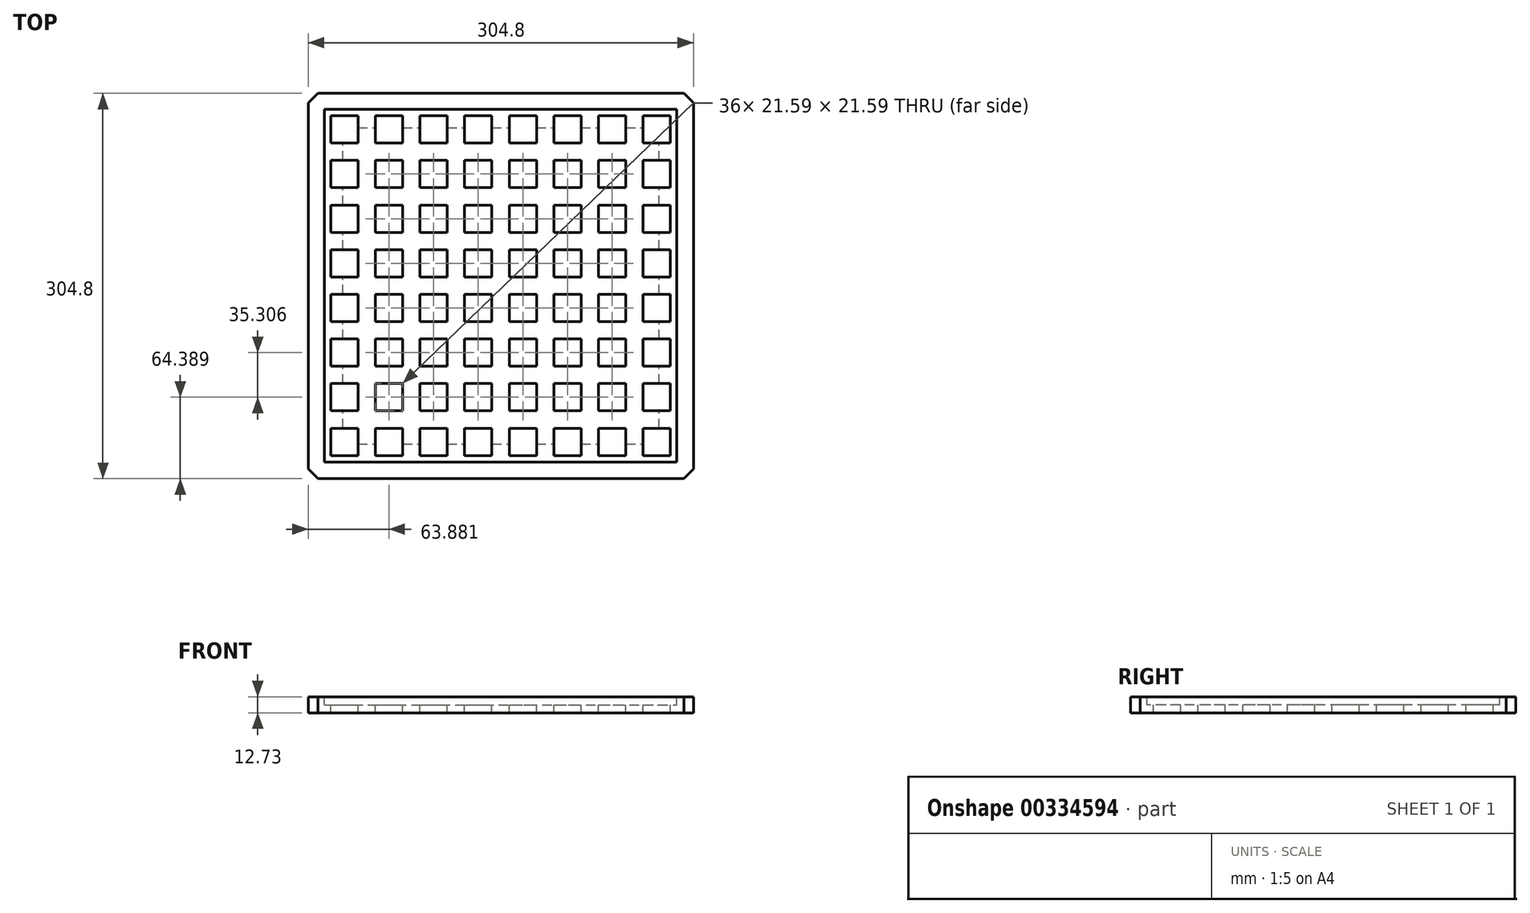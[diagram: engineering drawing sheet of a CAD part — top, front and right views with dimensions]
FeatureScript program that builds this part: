
annotation { "Feature Type Name" : "Feature", "Feature Type Description" : "" }
export const myFeature = defineFeature(function(context is Context, id is Id, definition is map)
    precondition{}
    {
        {
            var Q0;
            Q0=qCreatedBy(makeId("Top.planeOp"),FACE);
            var sketch = newSketch(context, id + "F0", { "sketchPlane" : qUnion([Q0])});
            skLineSegment(sketch, "E0.bottom", {"start": v(-152.4, 152.4) * mm, "end": v(152.4, 152.4) * mm});
            skLineSegment(sketch, "E0.top", {"start": v(-152.4, -152.4) * mm, "end": v(152.4, -152.4) * mm});
            skLineSegment(sketch, "E0.left", {"start": v(-152.4, 152.4) * mm, "end": v(-152.4, -152.4) * mm});
            skLineSegment(sketch, "E0.right", {"start": v(152.4, 152.4) * mm, "end": v(152.4, -152.4) * mm});
            skPoint(sketch, "E0.middle", {"position": v(0, 0) * mm});
            skSolve(sketch);
        }
        {
            var Q0;
            Q0=makeQuery(id+"F0.imprint","IMPRINT",FACE,{"disambiguationData":[TD([[makeQuery(id+"F0.imprint","IMPRINT",EDGE,{"derivedFrom":sQuery(id+"F0.wireOp",EDGE,"E0.bottom")}),-1.0]])]});
            extrude(context, id + "F1", {"entities" : qUnion([Q0]), "depth" : 12.7 * mm});
        }
        {
            var Q0;
            Q0=makeQuery(id+"F1.opExtrude","CAP_FACE",FACE,{"disambiguationData":[OSD([sQuery(id+"F0.wireOp",EDGE,"E0.bottom"),sQuery(id+"F0.wireOp",EDGE,"E0.top"),sQuery(id+"F0.wireOp",EDGE,"E0.left"),sQuery(id+"F0.wireOp",EDGE,"E0.right")])],"isStart":false});
            var sketch = newSketch(context, id + "F2", { "sketchPlane" : qUnion([Q0])});
            skLineSegment(sketch, "E1.top", {"start": v(-139.7, -139.7) * mm, "end": v(139.7, -139.7) * mm, "construction": true});
            skLineSegment(sketch, "E1.right", {"start": v(139.7, 139.7) * mm, "end": v(139.7, -139.7) * mm, "construction": true});
            skPoint(sketch, "E1.middle", {"position": v(0, 0) * mm});
            skLineSegment(sketch, "E2.bottom", {"start": v(-139.7, 139.7) * mm, "end": v(-107.95, 139.7) * mm});
            skLineSegment(sketch, "E2.top", {"start": v(-139.7, 107.95) * mm, "end": v(-107.95, 107.95) * mm});
            skLineSegment(sketch, "E2.left", {"start": v(-139.7, 139.7) * mm, "end": v(-139.7, 107.95) * mm});
            skLineSegment(sketch, "E2.right", {"start": v(-107.95, 139.7) * mm, "end": v(-107.95, 107.95) * mm});
            skLineSegment(sketch, "E3.1.0.0", {"start": v(-104.4, 139.7) * mm, "end": v(-72.64, 139.7) * mm});
            skLineSegment(sketch, "E3.1.0.1", {"start": v(-104.4, 107.95) * mm, "end": v(-72.64, 107.95) * mm});
            skLineSegment(sketch, "E3.1.0.2", {"start": v(-104.4, 139.7) * mm, "end": v(-104.4, 107.95) * mm});
            skLineSegment(sketch, "E3.1.0.3", {"start": v(-72.64, 139.7) * mm, "end": v(-72.64, 107.95) * mm});
            skLineSegment(sketch, "E3.2.0.0", {"start": v(-69.09, 139.7) * mm, "end": v(-37.34, 139.7) * mm});
            skLineSegment(sketch, "E3.2.0.1", {"start": v(-69.09, 107.95) * mm, "end": v(-37.34, 107.95) * mm});
            skLineSegment(sketch, "E3.2.0.2", {"start": v(-69.09, 139.7) * mm, "end": v(-69.09, 107.95) * mm});
            skLineSegment(sketch, "E3.2.0.3", {"start": v(-37.34, 139.7) * mm, "end": v(-37.34, 107.95) * mm});
            skLineSegment(sketch, "E3.3.0.0", {"start": v(-33.78, 139.7) * mm, "end": v(-2.03, 139.7) * mm});
            skLineSegment(sketch, "E3.3.0.1", {"start": v(-33.78, 107.95) * mm, "end": v(-2.03, 107.95) * mm});
            skLineSegment(sketch, "E3.3.0.2", {"start": v(-33.78, 139.7) * mm, "end": v(-33.78, 107.95) * mm});
            skLineSegment(sketch, "E3.3.0.3", {"start": v(-2.03, 139.7) * mm, "end": v(-2.03, 107.95) * mm});
            skLineSegment(sketch, "E3.4.0.0", {"start": v(1.52, 139.7) * mm, "end": v(33.27, 139.7) * mm});
            skLineSegment(sketch, "E3.4.0.1", {"start": v(1.52, 107.95) * mm, "end": v(33.27, 107.95) * mm});
            skLineSegment(sketch, "E3.4.0.2", {"start": v(1.52, 139.7) * mm, "end": v(1.52, 107.95) * mm});
            skLineSegment(sketch, "E3.4.0.3", {"start": v(33.27, 139.7) * mm, "end": v(33.27, 107.95) * mm});
            skLineSegment(sketch, "E3.5.0.0", {"start": v(36.83, 139.7) * mm, "end": v(68.58, 139.7) * mm});
            skLineSegment(sketch, "E3.5.0.1", {"start": v(36.83, 107.95) * mm, "end": v(68.58, 107.95) * mm});
            skLineSegment(sketch, "E3.5.0.2", {"start": v(36.83, 139.7) * mm, "end": v(36.83, 107.95) * mm});
            skLineSegment(sketch, "E3.5.0.3", {"start": v(68.58, 139.7) * mm, "end": v(68.58, 107.95) * mm});
            skLineSegment(sketch, "E3.6.0.0", {"start": v(72.14, 139.7) * mm, "end": v(103.89, 139.7) * mm});
            skLineSegment(sketch, "E3.6.0.1", {"start": v(72.14, 107.95) * mm, "end": v(103.89, 107.95) * mm});
            skLineSegment(sketch, "E3.6.0.2", {"start": v(72.14, 139.7) * mm, "end": v(72.14, 107.95) * mm});
            skLineSegment(sketch, "E3.6.0.3", {"start": v(103.89, 139.7) * mm, "end": v(103.89, 107.95) * mm});
            skLineSegment(sketch, "E3.7.0.0", {"start": v(107.44, 139.7) * mm, "end": v(139.2, 139.7) * mm});
            skLineSegment(sketch, "E3.7.0.1", {"start": v(107.44, 107.95) * mm, "end": v(139.2, 107.95) * mm});
            skLineSegment(sketch, "E3.7.0.2", {"start": v(107.44, 139.7) * mm, "end": v(107.44, 107.95) * mm});
            skLineSegment(sketch, "E3.7.0.3", {"start": v(139.2, 139.7) * mm, "end": v(139.2, 107.95) * mm});
            skLineSegment(sketch, "E3.direction1", {"start": v(-139.7, 107.95) * mm, "end": v(-104.4, 107.95) * mm, "construction": true});
            skLineSegment(sketch, "E4.0.1.0", {"start": v(-69.09, 104.4) * mm, "end": v(-37.34, 104.4) * mm});
            skLineSegment(sketch, "E4.0.1.1", {"start": v(-72.64, 104.4) * mm, "end": v(-72.64, 72.64) * mm});
            skLineSegment(sketch, "E4.0.1.2", {"start": v(1.52, 104.4) * mm, "end": v(33.27, 104.4) * mm});
            skLineSegment(sketch, "E4.0.1.3", {"start": v(-139.7, 72.64) * mm, "end": v(-104.4, 72.64) * mm, "construction": true});
            skLineSegment(sketch, "E4.0.1.4", {"start": v(-104.4, 104.4) * mm, "end": v(-104.4, 72.64) * mm});
            skLineSegment(sketch, "E4.0.1.5", {"start": v(-69.09, 72.64) * mm, "end": v(-37.34, 72.64) * mm});
            skLineSegment(sketch, "E4.0.1.6", {"start": v(107.44, 72.64) * mm, "end": v(139.2, 72.64) * mm});
            skLineSegment(sketch, "E4.0.1.7", {"start": v(36.83, 104.4) * mm, "end": v(68.58, 104.4) * mm});
            skLineSegment(sketch, "E4.0.1.8", {"start": v(68.58, 104.4) * mm, "end": v(68.58, 72.64) * mm});
            skLineSegment(sketch, "E4.0.1.9", {"start": v(-69.09, 104.4) * mm, "end": v(-69.09, 72.64) * mm});
            skLineSegment(sketch, "E4.0.1.10", {"start": v(-104.4, 72.64) * mm, "end": v(-72.64, 72.64) * mm});
            skLineSegment(sketch, "E4.0.1.11", {"start": v(-104.4, 104.4) * mm, "end": v(-72.64, 104.4) * mm});
            skLineSegment(sketch, "E4.0.1.12", {"start": v(-107.95, 104.4) * mm, "end": v(-107.95, 72.64) * mm});
            skLineSegment(sketch, "E4.0.1.13", {"start": v(-139.7, 104.4) * mm, "end": v(-139.7, 72.64) * mm});
            skLineSegment(sketch, "E4.0.1.14", {"start": v(-139.7, 104.4) * mm, "end": v(-107.95, 104.4) * mm});
            skLineSegment(sketch, "E4.0.1.15", {"start": v(-33.78, 72.64) * mm, "end": v(-2.03, 72.64) * mm});
            skLineSegment(sketch, "E4.0.1.16", {"start": v(-33.78, 104.4) * mm, "end": v(-2.03, 104.4) * mm});
            skLineSegment(sketch, "E4.0.1.17", {"start": v(-37.34, 104.4) * mm, "end": v(-37.34, 72.64) * mm});
            skLineSegment(sketch, "E4.0.1.18", {"start": v(1.52, 72.64) * mm, "end": v(33.27, 72.64) * mm});
            skLineSegment(sketch, "E4.0.1.19", {"start": v(72.14, 104.4) * mm, "end": v(103.89, 104.4) * mm});
            skLineSegment(sketch, "E4.0.1.20", {"start": v(-2.03, 104.4) * mm, "end": v(-2.03, 72.64) * mm});
            skLineSegment(sketch, "E4.0.1.21", {"start": v(139.2, 104.4) * mm, "end": v(139.2, 72.64) * mm});
            skLineSegment(sketch, "E4.0.1.22", {"start": v(33.27, 104.4) * mm, "end": v(33.27, 72.64) * mm});
            skLineSegment(sketch, "E4.0.1.23", {"start": v(107.44, 104.4) * mm, "end": v(139.2, 104.4) * mm});
            skLineSegment(sketch, "E4.0.1.24", {"start": v(36.83, 104.4) * mm, "end": v(36.83, 72.64) * mm});
            skLineSegment(sketch, "E4.0.1.25", {"start": v(72.14, 104.4) * mm, "end": v(72.14, 72.64) * mm});
            skLineSegment(sketch, "E4.0.1.26", {"start": v(72.14, 72.64) * mm, "end": v(103.89, 72.64) * mm});
            skLineSegment(sketch, "E4.0.1.27", {"start": v(36.83, 72.64) * mm, "end": v(68.58, 72.64) * mm});
            skLineSegment(sketch, "E4.0.1.28", {"start": v(103.89, 104.4) * mm, "end": v(103.89, 72.64) * mm});
            skLineSegment(sketch, "E4.0.1.29", {"start": v(1.52, 104.4) * mm, "end": v(1.52, 72.64) * mm});
            skLineSegment(sketch, "E4.0.1.30", {"start": v(107.44, 104.4) * mm, "end": v(107.44, 72.64) * mm});
            skLineSegment(sketch, "E4.0.1.31", {"start": v(-33.78, 104.4) * mm, "end": v(-33.78, 72.64) * mm});
            skLineSegment(sketch, "E4.0.1.32", {"start": v(-139.7, 72.64) * mm, "end": v(-107.95, 72.64) * mm});
            skLineSegment(sketch, "E4.0.2.0", {"start": v(-69.09, 69.09) * mm, "end": v(-37.34, 69.09) * mm});
            skLineSegment(sketch, "E4.0.2.1", {"start": v(-72.64, 69.09) * mm, "end": v(-72.64, 37.34) * mm});
            skLineSegment(sketch, "E4.0.2.2", {"start": v(1.52, 69.09) * mm, "end": v(33.27, 69.09) * mm});
            skLineSegment(sketch, "E4.0.2.3", {"start": v(-139.7, 37.34) * mm, "end": v(-104.4, 37.34) * mm, "construction": true});
            skLineSegment(sketch, "E4.0.2.4", {"start": v(-104.4, 69.09) * mm, "end": v(-104.4, 37.34) * mm});
            skLineSegment(sketch, "E4.0.2.5", {"start": v(-69.09, 37.34) * mm, "end": v(-37.34, 37.34) * mm});
            skLineSegment(sketch, "E4.0.2.6", {"start": v(107.44, 37.34) * mm, "end": v(139.2, 37.34) * mm});
            skLineSegment(sketch, "E4.0.2.7", {"start": v(36.83, 69.09) * mm, "end": v(68.58, 69.09) * mm});
            skLineSegment(sketch, "E4.0.2.8", {"start": v(68.58, 69.09) * mm, "end": v(68.58, 37.34) * mm});
            skLineSegment(sketch, "E4.0.2.9", {"start": v(-69.09, 69.09) * mm, "end": v(-69.09, 37.34) * mm});
            skLineSegment(sketch, "E4.0.2.10", {"start": v(-104.4, 37.34) * mm, "end": v(-72.64, 37.34) * mm});
            skLineSegment(sketch, "E4.0.2.11", {"start": v(-104.4, 69.09) * mm, "end": v(-72.64, 69.09) * mm});
            skLineSegment(sketch, "E4.0.2.12", {"start": v(-107.95, 69.09) * mm, "end": v(-107.95, 37.34) * mm});
            skLineSegment(sketch, "E4.0.2.13", {"start": v(-139.7, 69.09) * mm, "end": v(-139.7, 37.34) * mm});
            skLineSegment(sketch, "E4.0.2.14", {"start": v(-139.7, 69.09) * mm, "end": v(-107.95, 69.09) * mm});
            skLineSegment(sketch, "E4.0.2.15", {"start": v(-33.78, 37.34) * mm, "end": v(-2.03, 37.34) * mm});
            skLineSegment(sketch, "E4.0.2.16", {"start": v(-33.78, 69.09) * mm, "end": v(-2.03, 69.09) * mm});
            skLineSegment(sketch, "E4.0.2.17", {"start": v(-37.34, 69.09) * mm, "end": v(-37.34, 37.34) * mm});
            skLineSegment(sketch, "E4.0.2.18", {"start": v(1.52, 37.34) * mm, "end": v(33.27, 37.34) * mm});
            skLineSegment(sketch, "E4.0.2.19", {"start": v(72.14, 69.09) * mm, "end": v(103.89, 69.09) * mm});
            skLineSegment(sketch, "E4.0.2.20", {"start": v(-2.03, 69.09) * mm, "end": v(-2.03, 37.34) * mm});
            skLineSegment(sketch, "E4.0.2.21", {"start": v(139.2, 69.09) * mm, "end": v(139.2, 37.34) * mm});
            skLineSegment(sketch, "E4.0.2.22", {"start": v(33.27, 69.09) * mm, "end": v(33.27, 37.34) * mm});
            skLineSegment(sketch, "E4.0.2.23", {"start": v(107.44, 69.09) * mm, "end": v(139.2, 69.09) * mm});
            skLineSegment(sketch, "E4.0.2.24", {"start": v(36.83, 69.09) * mm, "end": v(36.83, 37.34) * mm});
            skLineSegment(sketch, "E4.0.2.25", {"start": v(72.14, 69.09) * mm, "end": v(72.14, 37.34) * mm});
            skLineSegment(sketch, "E4.0.2.26", {"start": v(72.14, 37.34) * mm, "end": v(103.89, 37.34) * mm});
            skLineSegment(sketch, "E4.0.2.27", {"start": v(36.83, 37.34) * mm, "end": v(68.58, 37.34) * mm});
            skLineSegment(sketch, "E4.0.2.28", {"start": v(103.89, 69.09) * mm, "end": v(103.89, 37.34) * mm});
            skLineSegment(sketch, "E4.0.2.29", {"start": v(1.52, 69.09) * mm, "end": v(1.52, 37.34) * mm});
            skLineSegment(sketch, "E4.0.2.30", {"start": v(107.44, 69.09) * mm, "end": v(107.44, 37.34) * mm});
            skLineSegment(sketch, "E4.0.2.31", {"start": v(-33.78, 69.09) * mm, "end": v(-33.78, 37.34) * mm});
            skLineSegment(sketch, "E4.0.2.32", {"start": v(-139.7, 37.34) * mm, "end": v(-107.95, 37.34) * mm});
            skLineSegment(sketch, "E4.0.3.0", {"start": v(-69.09, 33.78) * mm, "end": v(-37.34, 33.78) * mm});
            skLineSegment(sketch, "E4.0.3.1", {"start": v(-72.64, 33.78) * mm, "end": v(-72.64, 2.03) * mm});
            skLineSegment(sketch, "E4.0.3.2", {"start": v(1.52, 33.78) * mm, "end": v(33.27, 33.78) * mm});
            skLineSegment(sketch, "E4.0.3.3", {"start": v(-139.7, 2.03) * mm, "end": v(-104.4, 2.03) * mm, "construction": true});
            skLineSegment(sketch, "E4.0.3.4", {"start": v(-104.4, 33.78) * mm, "end": v(-104.4, 2.03) * mm});
            skLineSegment(sketch, "E4.0.3.5", {"start": v(-69.09, 2.03) * mm, "end": v(-37.34, 2.03) * mm});
            skLineSegment(sketch, "E4.0.3.6", {"start": v(107.44, 2.03) * mm, "end": v(139.2, 2.03) * mm});
            skLineSegment(sketch, "E4.0.3.7", {"start": v(36.83, 33.78) * mm, "end": v(68.58, 33.78) * mm});
            skLineSegment(sketch, "E4.0.3.8", {"start": v(68.58, 33.78) * mm, "end": v(68.58, 2.03) * mm});
            skLineSegment(sketch, "E4.0.3.9", {"start": v(-69.09, 33.78) * mm, "end": v(-69.09, 2.03) * mm});
            skLineSegment(sketch, "E4.0.3.10", {"start": v(-104.4, 2.03) * mm, "end": v(-72.64, 2.03) * mm});
            skLineSegment(sketch, "E4.0.3.11", {"start": v(-104.4, 33.78) * mm, "end": v(-72.64, 33.78) * mm});
            skLineSegment(sketch, "E4.0.3.12", {"start": v(-107.95, 33.78) * mm, "end": v(-107.95, 2.03) * mm});
            skLineSegment(sketch, "E4.0.3.13", {"start": v(-139.7, 33.78) * mm, "end": v(-139.7, 2.03) * mm});
            skLineSegment(sketch, "E4.0.3.14", {"start": v(-139.7, 33.78) * mm, "end": v(-107.95, 33.78) * mm});
            skLineSegment(sketch, "E4.0.3.15", {"start": v(-33.78, 2.03) * mm, "end": v(-2.03, 2.03) * mm});
            skLineSegment(sketch, "E4.0.3.16", {"start": v(-33.78, 33.78) * mm, "end": v(-2.03, 33.78) * mm});
            skLineSegment(sketch, "E4.0.3.17", {"start": v(-37.34, 33.78) * mm, "end": v(-37.34, 2.03) * mm});
            skLineSegment(sketch, "E4.0.3.18", {"start": v(1.52, 2.03) * mm, "end": v(33.27, 2.03) * mm});
            skLineSegment(sketch, "E4.0.3.19", {"start": v(72.14, 33.78) * mm, "end": v(103.89, 33.78) * mm});
            skLineSegment(sketch, "E4.0.3.20", {"start": v(-2.03, 33.78) * mm, "end": v(-2.03, 2.03) * mm});
            skLineSegment(sketch, "E4.0.3.21", {"start": v(139.2, 33.78) * mm, "end": v(139.2, 2.03) * mm});
            skLineSegment(sketch, "E4.0.3.22", {"start": v(33.27, 33.78) * mm, "end": v(33.27, 2.03) * mm});
            skLineSegment(sketch, "E4.0.3.23", {"start": v(107.44, 33.78) * mm, "end": v(139.2, 33.78) * mm});
            skLineSegment(sketch, "E4.0.3.24", {"start": v(36.83, 33.78) * mm, "end": v(36.83, 2.03) * mm});
            skLineSegment(sketch, "E4.0.3.25", {"start": v(72.14, 33.78) * mm, "end": v(72.14, 2.03) * mm});
            skLineSegment(sketch, "E4.0.3.26", {"start": v(72.14, 2.03) * mm, "end": v(103.89, 2.03) * mm});
            skLineSegment(sketch, "E4.0.3.27", {"start": v(36.83, 2.03) * mm, "end": v(68.58, 2.03) * mm});
            skLineSegment(sketch, "E4.0.3.28", {"start": v(103.89, 33.78) * mm, "end": v(103.89, 2.03) * mm});
            skLineSegment(sketch, "E4.0.3.29", {"start": v(1.52, 33.78) * mm, "end": v(1.52, 2.03) * mm});
            skLineSegment(sketch, "E4.0.3.30", {"start": v(107.44, 33.78) * mm, "end": v(107.44, 2.03) * mm});
            skLineSegment(sketch, "E4.0.3.31", {"start": v(-33.78, 33.78) * mm, "end": v(-33.78, 2.03) * mm});
            skLineSegment(sketch, "E4.0.3.32", {"start": v(-139.7, 2.03) * mm, "end": v(-107.95, 2.03) * mm});
            skLineSegment(sketch, "E4.0.4.0", {"start": v(-69.09, -1.52) * mm, "end": v(-37.34, -1.52) * mm});
            skLineSegment(sketch, "E4.0.4.1", {"start": v(-72.64, -1.52) * mm, "end": v(-72.64, -33.27) * mm});
            skLineSegment(sketch, "E4.0.4.2", {"start": v(1.52, -1.52) * mm, "end": v(33.27, -1.52) * mm});
            skLineSegment(sketch, "E4.0.4.3", {"start": v(-139.7, -33.27) * mm, "end": v(-104.4, -33.27) * mm, "construction": true});
            skLineSegment(sketch, "E4.0.4.4", {"start": v(-104.4, -1.52) * mm, "end": v(-104.4, -33.27) * mm});
            skLineSegment(sketch, "E4.0.4.5", {"start": v(-69.09, -33.27) * mm, "end": v(-37.34, -33.27) * mm});
            skLineSegment(sketch, "E4.0.4.6", {"start": v(107.44, -33.27) * mm, "end": v(139.2, -33.27) * mm});
            skLineSegment(sketch, "E4.0.4.7", {"start": v(36.83, -1.52) * mm, "end": v(68.58, -1.52) * mm});
            skLineSegment(sketch, "E4.0.4.8", {"start": v(68.58, -1.52) * mm, "end": v(68.58, -33.27) * mm});
            skLineSegment(sketch, "E4.0.4.9", {"start": v(-69.09, -1.52) * mm, "end": v(-69.09, -33.27) * mm});
            skLineSegment(sketch, "E4.0.4.10", {"start": v(-104.4, -33.27) * mm, "end": v(-72.64, -33.27) * mm});
            skLineSegment(sketch, "E4.0.4.11", {"start": v(-104.4, -1.52) * mm, "end": v(-72.64, -1.52) * mm});
            skLineSegment(sketch, "E4.0.4.12", {"start": v(-107.95, -1.52) * mm, "end": v(-107.95, -33.27) * mm});
            skLineSegment(sketch, "E4.0.4.13", {"start": v(-139.7, -1.52) * mm, "end": v(-139.7, -33.27) * mm});
            skLineSegment(sketch, "E4.0.4.14", {"start": v(-139.7, -1.52) * mm, "end": v(-107.95, -1.52) * mm});
            skLineSegment(sketch, "E4.0.4.15", {"start": v(-33.78, -33.27) * mm, "end": v(-2.03, -33.27) * mm});
            skLineSegment(sketch, "E4.0.4.16", {"start": v(-33.78, -1.52) * mm, "end": v(-2.03, -1.52) * mm});
            skLineSegment(sketch, "E4.0.4.17", {"start": v(-37.34, -1.52) * mm, "end": v(-37.34, -33.27) * mm});
            skLineSegment(sketch, "E4.0.4.18", {"start": v(1.52, -33.27) * mm, "end": v(33.27, -33.27) * mm});
            skLineSegment(sketch, "E4.0.4.19", {"start": v(72.14, -1.52) * mm, "end": v(103.89, -1.52) * mm});
            skLineSegment(sketch, "E4.0.4.20", {"start": v(-2.03, -1.52) * mm, "end": v(-2.03, -33.27) * mm});
            skLineSegment(sketch, "E4.0.4.21", {"start": v(139.2, -1.52) * mm, "end": v(139.2, -33.27) * mm});
            skLineSegment(sketch, "E4.0.4.22", {"start": v(33.27, -1.52) * mm, "end": v(33.27, -33.27) * mm});
            skLineSegment(sketch, "E4.0.4.23", {"start": v(107.44, -1.52) * mm, "end": v(139.2, -1.52) * mm});
            skLineSegment(sketch, "E4.0.4.24", {"start": v(36.83, -1.52) * mm, "end": v(36.83, -33.27) * mm});
            skLineSegment(sketch, "E4.0.4.25", {"start": v(72.14, -1.52) * mm, "end": v(72.14, -33.27) * mm});
            skLineSegment(sketch, "E4.0.4.26", {"start": v(72.14, -33.27) * mm, "end": v(103.89, -33.27) * mm});
            skLineSegment(sketch, "E4.0.4.27", {"start": v(36.83, -33.27) * mm, "end": v(68.58, -33.27) * mm});
            skLineSegment(sketch, "E4.0.4.28", {"start": v(103.89, -1.52) * mm, "end": v(103.89, -33.27) * mm});
            skLineSegment(sketch, "E4.0.4.29", {"start": v(1.52, -1.52) * mm, "end": v(1.52, -33.27) * mm});
            skLineSegment(sketch, "E4.0.4.30", {"start": v(107.44, -1.52) * mm, "end": v(107.44, -33.27) * mm});
            skLineSegment(sketch, "E4.0.4.31", {"start": v(-33.78, -1.52) * mm, "end": v(-33.78, -33.27) * mm});
            skLineSegment(sketch, "E4.0.4.32", {"start": v(-139.7, -33.27) * mm, "end": v(-107.95, -33.27) * mm});
            skLineSegment(sketch, "E4.0.5.0", {"start": v(-69.09, -36.83) * mm, "end": v(-37.34, -36.83) * mm});
            skLineSegment(sketch, "E4.0.5.1", {"start": v(-72.64, -36.83) * mm, "end": v(-72.64, -68.58) * mm});
            skLineSegment(sketch, "E4.0.5.2", {"start": v(1.52, -36.83) * mm, "end": v(33.27, -36.83) * mm});
            skLineSegment(sketch, "E4.0.5.3", {"start": v(-139.7, -68.58) * mm, "end": v(-104.4, -68.58) * mm, "construction": true});
            skLineSegment(sketch, "E4.0.5.4", {"start": v(-104.4, -36.83) * mm, "end": v(-104.4, -68.58) * mm});
            skLineSegment(sketch, "E4.0.5.5", {"start": v(-69.09, -68.58) * mm, "end": v(-37.34, -68.58) * mm});
            skLineSegment(sketch, "E4.0.5.6", {"start": v(107.44, -68.58) * mm, "end": v(139.2, -68.58) * mm});
            skLineSegment(sketch, "E4.0.5.7", {"start": v(36.83, -36.83) * mm, "end": v(68.58, -36.83) * mm});
            skLineSegment(sketch, "E4.0.5.8", {"start": v(68.58, -36.83) * mm, "end": v(68.58, -68.58) * mm});
            skLineSegment(sketch, "E4.0.5.9", {"start": v(-69.09, -36.83) * mm, "end": v(-69.09, -68.58) * mm});
            skLineSegment(sketch, "E4.0.5.10", {"start": v(-104.4, -68.58) * mm, "end": v(-72.64, -68.58) * mm});
            skLineSegment(sketch, "E4.0.5.11", {"start": v(-104.4, -36.83) * mm, "end": v(-72.64, -36.83) * mm});
            skLineSegment(sketch, "E4.0.5.12", {"start": v(-107.95, -36.83) * mm, "end": v(-107.95, -68.58) * mm});
            skLineSegment(sketch, "E4.0.5.13", {"start": v(-139.7, -36.83) * mm, "end": v(-139.7, -68.58) * mm});
            skLineSegment(sketch, "E4.0.5.14", {"start": v(-139.7, -36.83) * mm, "end": v(-107.95, -36.83) * mm});
            skLineSegment(sketch, "E4.0.5.15", {"start": v(-33.78, -68.58) * mm, "end": v(-2.03, -68.58) * mm});
            skLineSegment(sketch, "E4.0.5.16", {"start": v(-33.78, -36.83) * mm, "end": v(-2.03, -36.83) * mm});
            skLineSegment(sketch, "E4.0.5.17", {"start": v(-37.34, -36.83) * mm, "end": v(-37.34, -68.58) * mm});
            skLineSegment(sketch, "E4.0.5.18", {"start": v(1.52, -68.58) * mm, "end": v(33.27, -68.58) * mm});
            skLineSegment(sketch, "E4.0.5.19", {"start": v(72.14, -36.83) * mm, "end": v(103.89, -36.83) * mm});
            skLineSegment(sketch, "E4.0.5.20", {"start": v(-2.03, -36.83) * mm, "end": v(-2.03, -68.58) * mm});
            skLineSegment(sketch, "E4.0.5.21", {"start": v(139.2, -36.83) * mm, "end": v(139.2, -68.58) * mm});
            skLineSegment(sketch, "E4.0.5.22", {"start": v(33.27, -36.83) * mm, "end": v(33.27, -68.58) * mm});
            skLineSegment(sketch, "E4.0.5.23", {"start": v(107.44, -36.83) * mm, "end": v(139.2, -36.83) * mm});
            skLineSegment(sketch, "E4.0.5.24", {"start": v(36.83, -36.83) * mm, "end": v(36.83, -68.58) * mm});
            skLineSegment(sketch, "E4.0.5.25", {"start": v(72.14, -36.83) * mm, "end": v(72.14, -68.58) * mm});
            skLineSegment(sketch, "E4.0.5.26", {"start": v(72.14, -68.58) * mm, "end": v(103.89, -68.58) * mm});
            skLineSegment(sketch, "E4.0.5.27", {"start": v(36.83, -68.58) * mm, "end": v(68.58, -68.58) * mm});
            skLineSegment(sketch, "E4.0.5.28", {"start": v(103.89, -36.83) * mm, "end": v(103.89, -68.58) * mm});
            skLineSegment(sketch, "E4.0.5.29", {"start": v(1.52, -36.83) * mm, "end": v(1.52, -68.58) * mm});
            skLineSegment(sketch, "E4.0.5.30", {"start": v(107.44, -36.83) * mm, "end": v(107.44, -68.58) * mm});
            skLineSegment(sketch, "E4.0.5.31", {"start": v(-33.78, -36.83) * mm, "end": v(-33.78, -68.58) * mm});
            skLineSegment(sketch, "E4.0.5.32", {"start": v(-139.7, -68.58) * mm, "end": v(-107.95, -68.58) * mm});
            skLineSegment(sketch, "E4.0.6.0", {"start": v(-69.09, -72.14) * mm, "end": v(-37.34, -72.14) * mm});
            skLineSegment(sketch, "E4.0.6.1", {"start": v(-72.64, -72.14) * mm, "end": v(-72.64, -103.89) * mm});
            skLineSegment(sketch, "E4.0.6.2", {"start": v(1.52, -72.14) * mm, "end": v(33.27, -72.14) * mm});
            skLineSegment(sketch, "E4.0.6.3", {"start": v(-139.7, -103.89) * mm, "end": v(-104.4, -103.89) * mm, "construction": true});
            skLineSegment(sketch, "E4.0.6.4", {"start": v(-104.4, -72.14) * mm, "end": v(-104.4, -103.89) * mm});
            skLineSegment(sketch, "E4.0.6.5", {"start": v(-69.09, -103.89) * mm, "end": v(-37.34, -103.89) * mm});
            skLineSegment(sketch, "E4.0.6.6", {"start": v(107.44, -103.89) * mm, "end": v(139.2, -103.89) * mm});
            skLineSegment(sketch, "E4.0.6.7", {"start": v(36.83, -72.14) * mm, "end": v(68.58, -72.14) * mm});
            skLineSegment(sketch, "E4.0.6.8", {"start": v(68.58, -72.14) * mm, "end": v(68.58, -103.89) * mm});
            skLineSegment(sketch, "E4.0.6.9", {"start": v(-69.09, -72.14) * mm, "end": v(-69.09, -103.89) * mm});
            skLineSegment(sketch, "E4.0.6.10", {"start": v(-104.4, -103.89) * mm, "end": v(-72.64, -103.89) * mm});
            skLineSegment(sketch, "E4.0.6.11", {"start": v(-104.4, -72.14) * mm, "end": v(-72.64, -72.14) * mm});
            skLineSegment(sketch, "E4.0.6.12", {"start": v(-107.95, -72.14) * mm, "end": v(-107.95, -103.89) * mm});
            skLineSegment(sketch, "E4.0.6.13", {"start": v(-139.7, -72.14) * mm, "end": v(-139.7, -103.89) * mm});
            skLineSegment(sketch, "E4.0.6.14", {"start": v(-139.7, -72.14) * mm, "end": v(-107.95, -72.14) * mm});
            skLineSegment(sketch, "E4.0.6.15", {"start": v(-33.78, -103.89) * mm, "end": v(-2.03, -103.89) * mm});
            skLineSegment(sketch, "E4.0.6.16", {"start": v(-33.78, -72.14) * mm, "end": v(-2.03, -72.14) * mm});
            skLineSegment(sketch, "E4.0.6.17", {"start": v(-37.34, -72.14) * mm, "end": v(-37.34, -103.89) * mm});
            skLineSegment(sketch, "E4.0.6.18", {"start": v(1.52, -103.89) * mm, "end": v(33.27, -103.89) * mm});
            skLineSegment(sketch, "E4.0.6.19", {"start": v(72.14, -72.14) * mm, "end": v(103.89, -72.14) * mm});
            skLineSegment(sketch, "E4.0.6.20", {"start": v(-2.03, -72.14) * mm, "end": v(-2.03, -103.89) * mm});
            skLineSegment(sketch, "E4.0.6.21", {"start": v(139.2, -72.14) * mm, "end": v(139.2, -103.89) * mm});
            skLineSegment(sketch, "E4.0.6.22", {"start": v(33.27, -72.14) * mm, "end": v(33.27, -103.89) * mm});
            skLineSegment(sketch, "E4.0.6.23", {"start": v(107.44, -72.14) * mm, "end": v(139.2, -72.14) * mm});
            skLineSegment(sketch, "E4.0.6.24", {"start": v(36.83, -72.14) * mm, "end": v(36.83, -103.89) * mm});
            skLineSegment(sketch, "E4.0.6.25", {"start": v(72.14, -72.14) * mm, "end": v(72.14, -103.89) * mm});
            skLineSegment(sketch, "E4.0.6.26", {"start": v(72.14, -103.89) * mm, "end": v(103.89, -103.89) * mm});
            skLineSegment(sketch, "E4.0.6.27", {"start": v(36.83, -103.89) * mm, "end": v(68.58, -103.89) * mm});
            skLineSegment(sketch, "E4.0.6.28", {"start": v(103.89, -72.14) * mm, "end": v(103.89, -103.89) * mm});
            skLineSegment(sketch, "E4.0.6.29", {"start": v(1.52, -72.14) * mm, "end": v(1.52, -103.89) * mm});
            skLineSegment(sketch, "E4.0.6.30", {"start": v(107.44, -72.14) * mm, "end": v(107.44, -103.89) * mm});
            skLineSegment(sketch, "E4.0.6.31", {"start": v(-33.78, -72.14) * mm, "end": v(-33.78, -103.89) * mm});
            skLineSegment(sketch, "E4.0.6.32", {"start": v(-139.7, -103.89) * mm, "end": v(-107.95, -103.89) * mm});
            skLineSegment(sketch, "E4.0.7.0", {"start": v(-69.09, -107.44) * mm, "end": v(-37.34, -107.44) * mm});
            skLineSegment(sketch, "E4.0.7.1", {"start": v(-72.64, -107.44) * mm, "end": v(-72.64, -139.2) * mm});
            skLineSegment(sketch, "E4.0.7.2", {"start": v(1.52, -107.44) * mm, "end": v(33.27, -107.44) * mm});
            skLineSegment(sketch, "E4.0.7.3", {"start": v(-139.7, -139.2) * mm, "end": v(-104.4, -139.2) * mm, "construction": true});
            skLineSegment(sketch, "E4.0.7.4", {"start": v(-104.4, -107.44) * mm, "end": v(-104.4, -139.2) * mm});
            skLineSegment(sketch, "E4.0.7.5", {"start": v(-69.09, -139.2) * mm, "end": v(-37.34, -139.2) * mm});
            skLineSegment(sketch, "E4.0.7.6", {"start": v(107.44, -139.2) * mm, "end": v(139.2, -139.2) * mm});
            skLineSegment(sketch, "E4.0.7.7", {"start": v(36.83, -107.44) * mm, "end": v(68.58, -107.44) * mm});
            skLineSegment(sketch, "E4.0.7.8", {"start": v(68.58, -107.44) * mm, "end": v(68.58, -139.2) * mm});
            skLineSegment(sketch, "E4.0.7.9", {"start": v(-69.09, -107.44) * mm, "end": v(-69.09, -139.2) * mm});
            skLineSegment(sketch, "E4.0.7.10", {"start": v(-104.4, -139.2) * mm, "end": v(-72.64, -139.2) * mm});
            skLineSegment(sketch, "E4.0.7.11", {"start": v(-104.4, -107.44) * mm, "end": v(-72.64, -107.44) * mm});
            skLineSegment(sketch, "E4.0.7.12", {"start": v(-107.95, -107.44) * mm, "end": v(-107.95, -139.2) * mm});
            skLineSegment(sketch, "E4.0.7.13", {"start": v(-139.7, -107.44) * mm, "end": v(-139.7, -139.2) * mm});
            skLineSegment(sketch, "E4.0.7.14", {"start": v(-139.7, -107.44) * mm, "end": v(-107.95, -107.44) * mm});
            skLineSegment(sketch, "E4.0.7.15", {"start": v(-33.78, -139.2) * mm, "end": v(-2.03, -139.2) * mm});
            skLineSegment(sketch, "E4.0.7.16", {"start": v(-33.78, -107.44) * mm, "end": v(-2.03, -107.44) * mm});
            skLineSegment(sketch, "E4.0.7.17", {"start": v(-37.34, -107.44) * mm, "end": v(-37.34, -139.2) * mm});
            skLineSegment(sketch, "E4.0.7.18", {"start": v(1.52, -139.2) * mm, "end": v(33.27, -139.2) * mm});
            skLineSegment(sketch, "E4.0.7.19", {"start": v(72.14, -107.44) * mm, "end": v(103.89, -107.44) * mm});
            skLineSegment(sketch, "E4.0.7.20", {"start": v(-2.03, -107.44) * mm, "end": v(-2.03, -139.2) * mm});
            skLineSegment(sketch, "E4.0.7.21", {"start": v(139.2, -107.44) * mm, "end": v(139.2, -139.2) * mm});
            skLineSegment(sketch, "E4.0.7.22", {"start": v(33.27, -107.44) * mm, "end": v(33.27, -139.2) * mm});
            skLineSegment(sketch, "E4.0.7.23", {"start": v(107.44, -107.44) * mm, "end": v(139.2, -107.44) * mm});
            skLineSegment(sketch, "E4.0.7.24", {"start": v(36.83, -107.44) * mm, "end": v(36.83, -139.2) * mm});
            skLineSegment(sketch, "E4.0.7.25", {"start": v(72.14, -107.44) * mm, "end": v(72.14, -139.2) * mm});
            skLineSegment(sketch, "E4.0.7.26", {"start": v(72.14, -139.2) * mm, "end": v(103.89, -139.2) * mm});
            skLineSegment(sketch, "E4.0.7.27", {"start": v(36.83, -139.2) * mm, "end": v(68.58, -139.2) * mm});
            skLineSegment(sketch, "E4.0.7.28", {"start": v(103.89, -107.44) * mm, "end": v(103.89, -139.2) * mm});
            skLineSegment(sketch, "E4.0.7.29", {"start": v(1.52, -107.44) * mm, "end": v(1.52, -139.2) * mm});
            skLineSegment(sketch, "E4.0.7.30", {"start": v(107.44, -107.44) * mm, "end": v(107.44, -139.2) * mm});
            skLineSegment(sketch, "E4.0.7.31", {"start": v(-33.78, -107.44) * mm, "end": v(-33.78, -139.2) * mm});
            skLineSegment(sketch, "E4.0.7.32", {"start": v(-139.7, -139.2) * mm, "end": v(-107.95, -139.2) * mm});
            skLineSegment(sketch, "E4.direction1", {"start": v(-139.7, 107.95) * mm, "end": v(-114.3, 107.95) * mm, "construction": true});
            skLineSegment(sketch, "E4.direction2", {"start": v(-139.7, 107.95) * mm, "end": v(-139.7, 72.64) * mm, "construction": true});
            skSolve(sketch);
        }
        {
            var Q0;
            Q0 = qSketchRegion(id + "F2", true);
            extrude(context, id + "F3", {"entities" : qUnion([Q0]), "operationType" : NewBodyOperationType.REMOVE, "oppositeDirection" : true, "depth" : 6.35 * mm});
        }
        {
            var Q0;
            Q0=makeQuery(id+"F3.boolean.opBoolean","COPY",FACE,{"derivedFrom":makeQuery(id+"F3.opExtrude","CAP_FACE",FACE,{"disambiguationData":[OSD([sQuery(id+"F2.wireOp",EDGE,"E2.bottom"),sQuery(id+"F2.wireOp",EDGE,"E2.top"),sQuery(id+"F2.wireOp",EDGE,"E2.left"),sQuery(id+"F2.wireOp",EDGE,"E2.right")])],"isStart":false})});
            var sketch = newSketch(context, id + "F4", { "sketchPlane" : qUnion([Q0])});
            skLineSegment(sketch, "E5.bottom", {"start": v(-134.62, 134.62) * mm, "end": v(-113.03, 134.62) * mm});
            skLineSegment(sketch, "E5.top", {"start": v(-134.62, 113.03) * mm, "end": v(-113.03, 113.03) * mm});
            skLineSegment(sketch, "E5.left", {"start": v(-134.62, 134.62) * mm, "end": v(-134.62, 113.03) * mm});
            skLineSegment(sketch, "E5.right", {"start": v(-113.03, 134.62) * mm, "end": v(-113.03, 113.03) * mm});
            skPoint(sketch, "E5.middle", {"position": v(-123.83, 123.82) * mm});
            skPoint(sketch, "E5.middle.positionSnap0", {"position": v(-123.83, 107.95) * mm});
            skPoint(sketch, "E5.middle.positionSnap1", {"position": v(-107.95, 123.82) * mm});
            skPoint(sketch, "E5.centerSnap0", {"position": v(-123.83, 107.95) * mm});
            skPoint(sketch, "E5.centerSnap1", {"position": v(-107.95, 123.82) * mm});
            skPoint(sketch, "E6.0.1.0", {"position": v(-123.83, 88.52) * mm});
            skLineSegment(sketch, "E6.0.1.1", {"start": v(-134.62, 77.72) * mm, "end": v(-113.03, 77.72) * mm});
            skLineSegment(sketch, "E6.0.1.2", {"start": v(-134.62, 99.31) * mm, "end": v(-113.03, 99.31) * mm});
            skLineSegment(sketch, "E6.0.1.3", {"start": v(-113.03, 99.31) * mm, "end": v(-113.03, 77.72) * mm});
            skLineSegment(sketch, "E6.0.1.4", {"start": v(-134.62, 99.31) * mm, "end": v(-134.62, 77.72) * mm});
            skPoint(sketch, "E6.0.2.0", {"position": v(-123.83, 53.21) * mm});
            skLineSegment(sketch, "E6.0.2.1", {"start": v(-134.62, 42.42) * mm, "end": v(-113.03, 42.42) * mm});
            skLineSegment(sketch, "E6.0.2.2", {"start": v(-134.62, 64) * mm, "end": v(-113.03, 64) * mm});
            skLineSegment(sketch, "E6.0.2.3", {"start": v(-113.03, 64) * mm, "end": v(-113.03, 42.42) * mm});
            skLineSegment(sketch, "E6.0.2.4", {"start": v(-134.62, 64) * mm, "end": v(-134.62, 42.42) * mm});
            skPoint(sketch, "E6.0.3.0", {"position": v(-123.83, 17.9) * mm});
            skLineSegment(sketch, "E6.0.3.1", {"start": v(-134.62, 7.11) * mm, "end": v(-113.03, 7.11) * mm});
            skLineSegment(sketch, "E6.0.3.2", {"start": v(-134.62, 28.7) * mm, "end": v(-113.03, 28.7) * mm});
            skLineSegment(sketch, "E6.0.3.3", {"start": v(-113.03, 28.7) * mm, "end": v(-113.03, 7.11) * mm});
            skLineSegment(sketch, "E6.0.3.4", {"start": v(-134.62, 28.7) * mm, "end": v(-134.62, 7.11) * mm});
            skPoint(sketch, "E6.0.4.0", {"position": v(-123.83, -17.4) * mm});
            skLineSegment(sketch, "E6.0.4.1", {"start": v(-134.62, -28.2) * mm, "end": v(-113.03, -28.2) * mm});
            skLineSegment(sketch, "E6.0.4.2", {"start": v(-134.62, -6.6) * mm, "end": v(-113.03, -6.6) * mm});
            skLineSegment(sketch, "E6.0.4.3", {"start": v(-113.03, -6.6) * mm, "end": v(-113.03, -28.2) * mm});
            skLineSegment(sketch, "E6.0.4.4", {"start": v(-134.62, -6.6) * mm, "end": v(-134.62, -28.2) * mm});
            skPoint(sketch, "E6.0.5.0", {"position": v(-123.83, -52.7) * mm});
            skLineSegment(sketch, "E6.0.5.1", {"start": v(-134.62, -63.5) * mm, "end": v(-113.03, -63.5) * mm});
            skLineSegment(sketch, "E6.0.5.2", {"start": v(-134.62, -41.91) * mm, "end": v(-113.03, -41.91) * mm});
            skLineSegment(sketch, "E6.0.5.3", {"start": v(-113.03, -41.91) * mm, "end": v(-113.03, -63.5) * mm});
            skLineSegment(sketch, "E6.0.5.4", {"start": v(-134.62, -41.91) * mm, "end": v(-134.62, -63.5) * mm});
            skPoint(sketch, "E6.0.6.0", {"position": v(-123.83, -88.01) * mm});
            skLineSegment(sketch, "E6.0.6.1", {"start": v(-134.62, -98.8) * mm, "end": v(-113.03, -98.8) * mm});
            skLineSegment(sketch, "E6.0.6.2", {"start": v(-134.62, -77.22) * mm, "end": v(-113.03, -77.22) * mm});
            skLineSegment(sketch, "E6.0.6.3", {"start": v(-113.03, -77.22) * mm, "end": v(-113.03, -98.8) * mm});
            skLineSegment(sketch, "E6.0.6.4", {"start": v(-134.62, -77.22) * mm, "end": v(-134.62, -98.8) * mm});
            skPoint(sketch, "E6.0.7.0", {"position": v(-123.83, -123.32) * mm});
            skLineSegment(sketch, "E6.0.7.1", {"start": v(-134.62, -134.11) * mm, "end": v(-113.03, -134.11) * mm});
            skLineSegment(sketch, "E6.0.7.2", {"start": v(-134.62, -112.52) * mm, "end": v(-113.03, -112.52) * mm});
            skLineSegment(sketch, "E6.0.7.3", {"start": v(-113.03, -112.52) * mm, "end": v(-113.03, -134.11) * mm});
            skLineSegment(sketch, "E6.0.7.4", {"start": v(-134.62, -112.52) * mm, "end": v(-134.62, -134.11) * mm});
            skPoint(sketch, "E6.1.0.0", {"position": v(-88.52, 123.82) * mm});
            skLineSegment(sketch, "E6.1.0.1", {"start": v(-99.31, 113.03) * mm, "end": v(-77.72, 113.03) * mm});
            skLineSegment(sketch, "E6.1.0.2", {"start": v(-99.31, 134.62) * mm, "end": v(-77.72, 134.62) * mm});
            skLineSegment(sketch, "E6.1.0.3", {"start": v(-77.72, 134.62) * mm, "end": v(-77.72, 113.03) * mm});
            skLineSegment(sketch, "E6.1.0.4", {"start": v(-99.31, 134.62) * mm, "end": v(-99.31, 113.03) * mm});
            skPoint(sketch, "E6.1.1.0", {"position": v(-88.52, 88.52) * mm});
            skLineSegment(sketch, "E6.1.1.1", {"start": v(-99.31, 77.72) * mm, "end": v(-77.72, 77.72) * mm});
            skLineSegment(sketch, "E6.1.1.2", {"start": v(-99.31, 99.31) * mm, "end": v(-77.72, 99.31) * mm});
            skLineSegment(sketch, "E6.1.1.3", {"start": v(-77.72, 99.31) * mm, "end": v(-77.72, 77.72) * mm});
            skLineSegment(sketch, "E6.1.1.4", {"start": v(-99.31, 99.31) * mm, "end": v(-99.31, 77.72) * mm});
            skPoint(sketch, "E6.1.2.0", {"position": v(-88.52, 53.21) * mm});
            skLineSegment(sketch, "E6.1.2.1", {"start": v(-99.31, 42.42) * mm, "end": v(-77.72, 42.42) * mm});
            skLineSegment(sketch, "E6.1.2.2", {"start": v(-99.31, 64) * mm, "end": v(-77.72, 64) * mm});
            skLineSegment(sketch, "E6.1.2.3", {"start": v(-77.72, 64) * mm, "end": v(-77.72, 42.42) * mm});
            skLineSegment(sketch, "E6.1.2.4", {"start": v(-99.31, 64) * mm, "end": v(-99.31, 42.42) * mm});
            skPoint(sketch, "E6.1.3.0", {"position": v(-88.52, 17.9) * mm});
            skLineSegment(sketch, "E6.1.3.1", {"start": v(-99.31, 7.11) * mm, "end": v(-77.72, 7.11) * mm});
            skLineSegment(sketch, "E6.1.3.2", {"start": v(-99.31, 28.7) * mm, "end": v(-77.72, 28.7) * mm});
            skLineSegment(sketch, "E6.1.3.3", {"start": v(-77.72, 28.7) * mm, "end": v(-77.72, 7.11) * mm});
            skLineSegment(sketch, "E6.1.3.4", {"start": v(-99.31, 28.7) * mm, "end": v(-99.31, 7.11) * mm});
            skPoint(sketch, "E6.1.4.0", {"position": v(-88.52, -17.4) * mm});
            skLineSegment(sketch, "E6.1.4.1", {"start": v(-99.31, -28.2) * mm, "end": v(-77.72, -28.2) * mm});
            skLineSegment(sketch, "E6.1.4.2", {"start": v(-99.31, -6.6) * mm, "end": v(-77.72, -6.6) * mm});
            skLineSegment(sketch, "E6.1.4.3", {"start": v(-77.72, -6.6) * mm, "end": v(-77.72, -28.2) * mm});
            skLineSegment(sketch, "E6.1.4.4", {"start": v(-99.31, -6.6) * mm, "end": v(-99.31, -28.2) * mm});
            skPoint(sketch, "E6.1.5.0", {"position": v(-88.52, -52.7) * mm});
            skLineSegment(sketch, "E6.1.5.1", {"start": v(-99.31, -63.5) * mm, "end": v(-77.72, -63.5) * mm});
            skLineSegment(sketch, "E6.1.5.2", {"start": v(-99.31, -41.91) * mm, "end": v(-77.72, -41.91) * mm});
            skLineSegment(sketch, "E6.1.5.3", {"start": v(-77.72, -41.91) * mm, "end": v(-77.72, -63.5) * mm});
            skLineSegment(sketch, "E6.1.5.4", {"start": v(-99.31, -41.91) * mm, "end": v(-99.31, -63.5) * mm});
            skPoint(sketch, "E6.1.6.0", {"position": v(-88.52, -88.01) * mm});
            skLineSegment(sketch, "E6.1.6.1", {"start": v(-99.31, -98.8) * mm, "end": v(-77.72, -98.8) * mm});
            skLineSegment(sketch, "E6.1.6.2", {"start": v(-99.31, -77.22) * mm, "end": v(-77.72, -77.22) * mm});
            skLineSegment(sketch, "E6.1.6.3", {"start": v(-77.72, -77.22) * mm, "end": v(-77.72, -98.8) * mm});
            skLineSegment(sketch, "E6.1.6.4", {"start": v(-99.31, -77.22) * mm, "end": v(-99.31, -98.8) * mm});
            skPoint(sketch, "E6.1.7.0", {"position": v(-88.52, -123.32) * mm});
            skLineSegment(sketch, "E6.1.7.1", {"start": v(-99.31, -134.11) * mm, "end": v(-77.72, -134.11) * mm});
            skLineSegment(sketch, "E6.1.7.2", {"start": v(-99.31, -112.52) * mm, "end": v(-77.72, -112.52) * mm});
            skLineSegment(sketch, "E6.1.7.3", {"start": v(-77.72, -112.52) * mm, "end": v(-77.72, -134.11) * mm});
            skLineSegment(sketch, "E6.1.7.4", {"start": v(-99.31, -112.52) * mm, "end": v(-99.31, -134.11) * mm});
            skPoint(sketch, "E6.2.0.0", {"position": v(-53.21, 123.82) * mm});
            skLineSegment(sketch, "E6.2.0.1", {"start": v(-64, 113.03) * mm, "end": v(-42.42, 113.03) * mm});
            skLineSegment(sketch, "E6.2.0.2", {"start": v(-64, 134.62) * mm, "end": v(-42.42, 134.62) * mm});
            skLineSegment(sketch, "E6.2.0.3", {"start": v(-42.42, 134.62) * mm, "end": v(-42.42, 113.03) * mm});
            skLineSegment(sketch, "E6.2.0.4", {"start": v(-64, 134.62) * mm, "end": v(-64, 113.03) * mm});
            skPoint(sketch, "E6.2.1.0", {"position": v(-53.21, 88.52) * mm});
            skLineSegment(sketch, "E6.2.1.1", {"start": v(-64, 77.72) * mm, "end": v(-42.42, 77.72) * mm});
            skLineSegment(sketch, "E6.2.1.2", {"start": v(-64, 99.31) * mm, "end": v(-42.42, 99.31) * mm});
            skLineSegment(sketch, "E6.2.1.3", {"start": v(-42.42, 99.31) * mm, "end": v(-42.42, 77.72) * mm});
            skLineSegment(sketch, "E6.2.1.4", {"start": v(-64, 99.31) * mm, "end": v(-64, 77.72) * mm});
            skPoint(sketch, "E6.2.2.0", {"position": v(-53.21, 53.21) * mm});
            skLineSegment(sketch, "E6.2.2.1", {"start": v(-64, 42.42) * mm, "end": v(-42.42, 42.42) * mm});
            skLineSegment(sketch, "E6.2.2.2", {"start": v(-64, 64) * mm, "end": v(-42.42, 64) * mm});
            skLineSegment(sketch, "E6.2.2.3", {"start": v(-42.42, 64) * mm, "end": v(-42.42, 42.42) * mm});
            skLineSegment(sketch, "E6.2.2.4", {"start": v(-64, 64) * mm, "end": v(-64, 42.42) * mm});
            skPoint(sketch, "E6.2.3.0", {"position": v(-53.21, 17.9) * mm});
            skLineSegment(sketch, "E6.2.3.1", {"start": v(-64, 7.11) * mm, "end": v(-42.42, 7.11) * mm});
            skLineSegment(sketch, "E6.2.3.2", {"start": v(-64, 28.7) * mm, "end": v(-42.42, 28.7) * mm});
            skLineSegment(sketch, "E6.2.3.3", {"start": v(-42.42, 28.7) * mm, "end": v(-42.42, 7.11) * mm});
            skLineSegment(sketch, "E6.2.3.4", {"start": v(-64, 28.7) * mm, "end": v(-64, 7.11) * mm});
            skPoint(sketch, "E6.2.4.0", {"position": v(-53.21, -17.4) * mm});
            skLineSegment(sketch, "E6.2.4.1", {"start": v(-64, -28.2) * mm, "end": v(-42.42, -28.2) * mm});
            skLineSegment(sketch, "E6.2.4.2", {"start": v(-64, -6.6) * mm, "end": v(-42.42, -6.6) * mm});
            skLineSegment(sketch, "E6.2.4.3", {"start": v(-42.42, -6.6) * mm, "end": v(-42.42, -28.2) * mm});
            skLineSegment(sketch, "E6.2.4.4", {"start": v(-64, -6.6) * mm, "end": v(-64, -28.2) * mm});
            skPoint(sketch, "E6.2.5.0", {"position": v(-53.21, -52.7) * mm});
            skLineSegment(sketch, "E6.2.5.1", {"start": v(-64, -63.5) * mm, "end": v(-42.42, -63.5) * mm});
            skLineSegment(sketch, "E6.2.5.2", {"start": v(-64, -41.91) * mm, "end": v(-42.42, -41.91) * mm});
            skLineSegment(sketch, "E6.2.5.3", {"start": v(-42.42, -41.91) * mm, "end": v(-42.42, -63.5) * mm});
            skLineSegment(sketch, "E6.2.5.4", {"start": v(-64, -41.91) * mm, "end": v(-64, -63.5) * mm});
            skPoint(sketch, "E6.2.6.0", {"position": v(-53.21, -88.01) * mm});
            skLineSegment(sketch, "E6.2.6.1", {"start": v(-64, -98.8) * mm, "end": v(-42.42, -98.8) * mm});
            skLineSegment(sketch, "E6.2.6.2", {"start": v(-64, -77.22) * mm, "end": v(-42.42, -77.22) * mm});
            skLineSegment(sketch, "E6.2.6.3", {"start": v(-42.42, -77.22) * mm, "end": v(-42.42, -98.8) * mm});
            skLineSegment(sketch, "E6.2.6.4", {"start": v(-64, -77.22) * mm, "end": v(-64, -98.8) * mm});
            skPoint(sketch, "E6.2.7.0", {"position": v(-53.21, -123.32) * mm});
            skLineSegment(sketch, "E6.2.7.1", {"start": v(-64, -134.11) * mm, "end": v(-42.42, -134.11) * mm});
            skLineSegment(sketch, "E6.2.7.2", {"start": v(-64, -112.52) * mm, "end": v(-42.42, -112.52) * mm});
            skLineSegment(sketch, "E6.2.7.3", {"start": v(-42.42, -112.52) * mm, "end": v(-42.42, -134.11) * mm});
            skLineSegment(sketch, "E6.2.7.4", {"start": v(-64, -112.52) * mm, "end": v(-64, -134.11) * mm});
            skPoint(sketch, "E6.3.0.0", {"position": v(-17.9, 123.82) * mm});
            skLineSegment(sketch, "E6.3.0.1", {"start": v(-28.7, 113.03) * mm, "end": v(-7.11, 113.03) * mm});
            skLineSegment(sketch, "E6.3.0.2", {"start": v(-28.7, 134.62) * mm, "end": v(-7.11, 134.62) * mm});
            skLineSegment(sketch, "E6.3.0.3", {"start": v(-7.11, 134.62) * mm, "end": v(-7.11, 113.03) * mm});
            skLineSegment(sketch, "E6.3.0.4", {"start": v(-28.7, 134.62) * mm, "end": v(-28.7, 113.03) * mm});
            skPoint(sketch, "E6.3.1.0", {"position": v(-17.9, 88.52) * mm});
            skLineSegment(sketch, "E6.3.1.1", {"start": v(-28.7, 77.72) * mm, "end": v(-7.11, 77.72) * mm});
            skLineSegment(sketch, "E6.3.1.2", {"start": v(-28.7, 99.31) * mm, "end": v(-7.11, 99.31) * mm});
            skLineSegment(sketch, "E6.3.1.3", {"start": v(-7.11, 99.31) * mm, "end": v(-7.11, 77.72) * mm});
            skLineSegment(sketch, "E6.3.1.4", {"start": v(-28.7, 99.31) * mm, "end": v(-28.7, 77.72) * mm});
            skPoint(sketch, "E6.3.2.0", {"position": v(-17.9, 53.21) * mm});
            skLineSegment(sketch, "E6.3.2.1", {"start": v(-28.7, 42.42) * mm, "end": v(-7.11, 42.42) * mm});
            skLineSegment(sketch, "E6.3.2.2", {"start": v(-28.7, 64) * mm, "end": v(-7.11, 64) * mm});
            skLineSegment(sketch, "E6.3.2.3", {"start": v(-7.11, 64) * mm, "end": v(-7.11, 42.42) * mm});
            skLineSegment(sketch, "E6.3.2.4", {"start": v(-28.7, 64) * mm, "end": v(-28.7, 42.42) * mm});
            skPoint(sketch, "E6.3.3.0", {"position": v(-17.9, 17.9) * mm});
            skLineSegment(sketch, "E6.3.3.1", {"start": v(-28.7, 7.11) * mm, "end": v(-7.11, 7.11) * mm});
            skLineSegment(sketch, "E6.3.3.2", {"start": v(-28.7, 28.7) * mm, "end": v(-7.11, 28.7) * mm});
            skLineSegment(sketch, "E6.3.3.3", {"start": v(-7.11, 28.7) * mm, "end": v(-7.11, 7.11) * mm});
            skLineSegment(sketch, "E6.3.3.4", {"start": v(-28.7, 28.7) * mm, "end": v(-28.7, 7.11) * mm});
            skPoint(sketch, "E6.3.4.0", {"position": v(-17.9, -17.4) * mm});
            skLineSegment(sketch, "E6.3.4.1", {"start": v(-28.7, -28.2) * mm, "end": v(-7.11, -28.2) * mm});
            skLineSegment(sketch, "E6.3.4.2", {"start": v(-28.7, -6.6) * mm, "end": v(-7.11, -6.6) * mm});
            skLineSegment(sketch, "E6.3.4.3", {"start": v(-7.11, -6.6) * mm, "end": v(-7.11, -28.2) * mm});
            skLineSegment(sketch, "E6.3.4.4", {"start": v(-28.7, -6.6) * mm, "end": v(-28.7, -28.2) * mm});
            skPoint(sketch, "E6.3.5.0", {"position": v(-17.9, -52.7) * mm});
            skLineSegment(sketch, "E6.3.5.1", {"start": v(-28.7, -63.5) * mm, "end": v(-7.11, -63.5) * mm});
            skLineSegment(sketch, "E6.3.5.2", {"start": v(-28.7, -41.91) * mm, "end": v(-7.11, -41.91) * mm});
            skLineSegment(sketch, "E6.3.5.3", {"start": v(-7.11, -41.91) * mm, "end": v(-7.11, -63.5) * mm});
            skLineSegment(sketch, "E6.3.5.4", {"start": v(-28.7, -41.91) * mm, "end": v(-28.7, -63.5) * mm});
            skPoint(sketch, "E6.3.6.0", {"position": v(-17.9, -88.01) * mm});
            skLineSegment(sketch, "E6.3.6.1", {"start": v(-28.7, -98.8) * mm, "end": v(-7.11, -98.8) * mm});
            skLineSegment(sketch, "E6.3.6.2", {"start": v(-28.7, -77.22) * mm, "end": v(-7.11, -77.22) * mm});
            skLineSegment(sketch, "E6.3.6.3", {"start": v(-7.11, -77.22) * mm, "end": v(-7.11, -98.8) * mm});
            skLineSegment(sketch, "E6.3.6.4", {"start": v(-28.7, -77.22) * mm, "end": v(-28.7, -98.8) * mm});
            skPoint(sketch, "E6.3.7.0", {"position": v(-17.9, -123.32) * mm});
            skLineSegment(sketch, "E6.3.7.1", {"start": v(-28.7, -134.11) * mm, "end": v(-7.11, -134.11) * mm});
            skLineSegment(sketch, "E6.3.7.2", {"start": v(-28.7, -112.52) * mm, "end": v(-7.11, -112.52) * mm});
            skLineSegment(sketch, "E6.3.7.3", {"start": v(-7.11, -112.52) * mm, "end": v(-7.11, -134.11) * mm});
            skLineSegment(sketch, "E6.3.7.4", {"start": v(-28.7, -112.52) * mm, "end": v(-28.7, -134.11) * mm});
            skPoint(sketch, "E6.4.0.0", {"position": v(17.4, 123.82) * mm});
            skLineSegment(sketch, "E6.4.0.1", {"start": v(6.6, 113.03) * mm, "end": v(28.2, 113.03) * mm});
            skLineSegment(sketch, "E6.4.0.2", {"start": v(6.6, 134.62) * mm, "end": v(28.2, 134.62) * mm});
            skLineSegment(sketch, "E6.4.0.3", {"start": v(28.2, 134.62) * mm, "end": v(28.2, 113.03) * mm});
            skLineSegment(sketch, "E6.4.0.4", {"start": v(6.6, 134.62) * mm, "end": v(6.6, 113.03) * mm});
            skPoint(sketch, "E6.4.1.0", {"position": v(17.4, 88.52) * mm});
            skLineSegment(sketch, "E6.4.1.1", {"start": v(6.6, 77.72) * mm, "end": v(28.2, 77.72) * mm});
            skLineSegment(sketch, "E6.4.1.2", {"start": v(6.6, 99.31) * mm, "end": v(28.2, 99.31) * mm});
            skLineSegment(sketch, "E6.4.1.3", {"start": v(28.2, 99.31) * mm, "end": v(28.2, 77.72) * mm});
            skLineSegment(sketch, "E6.4.1.4", {"start": v(6.6, 99.31) * mm, "end": v(6.6, 77.72) * mm});
            skPoint(sketch, "E6.4.2.0", {"position": v(17.4, 53.21) * mm});
            skLineSegment(sketch, "E6.4.2.1", {"start": v(6.6, 42.42) * mm, "end": v(28.2, 42.42) * mm});
            skLineSegment(sketch, "E6.4.2.2", {"start": v(6.6, 64) * mm, "end": v(28.2, 64) * mm});
            skLineSegment(sketch, "E6.4.2.3", {"start": v(28.2, 64) * mm, "end": v(28.2, 42.42) * mm});
            skLineSegment(sketch, "E6.4.2.4", {"start": v(6.6, 64) * mm, "end": v(6.6, 42.42) * mm});
            skPoint(sketch, "E6.4.3.0", {"position": v(17.4, 17.9) * mm});
            skLineSegment(sketch, "E6.4.3.1", {"start": v(6.6, 7.11) * mm, "end": v(28.2, 7.11) * mm});
            skLineSegment(sketch, "E6.4.3.2", {"start": v(6.6, 28.7) * mm, "end": v(28.2, 28.7) * mm});
            skLineSegment(sketch, "E6.4.3.3", {"start": v(28.2, 28.7) * mm, "end": v(28.2, 7.11) * mm});
            skLineSegment(sketch, "E6.4.3.4", {"start": v(6.6, 28.7) * mm, "end": v(6.6, 7.11) * mm});
            skPoint(sketch, "E6.4.4.0", {"position": v(17.4, -17.4) * mm});
            skLineSegment(sketch, "E6.4.4.1", {"start": v(6.6, -28.2) * mm, "end": v(28.2, -28.2) * mm});
            skLineSegment(sketch, "E6.4.4.2", {"start": v(6.6, -6.6) * mm, "end": v(28.2, -6.6) * mm});
            skLineSegment(sketch, "E6.4.4.3", {"start": v(28.2, -6.6) * mm, "end": v(28.2, -28.2) * mm});
            skLineSegment(sketch, "E6.4.4.4", {"start": v(6.6, -6.6) * mm, "end": v(6.6, -28.2) * mm});
            skPoint(sketch, "E6.4.5.0", {"position": v(17.4, -52.7) * mm});
            skLineSegment(sketch, "E6.4.5.1", {"start": v(6.6, -63.5) * mm, "end": v(28.2, -63.5) * mm});
            skLineSegment(sketch, "E6.4.5.2", {"start": v(6.6, -41.91) * mm, "end": v(28.2, -41.91) * mm});
            skLineSegment(sketch, "E6.4.5.3", {"start": v(28.2, -41.91) * mm, "end": v(28.2, -63.5) * mm});
            skLineSegment(sketch, "E6.4.5.4", {"start": v(6.6, -41.91) * mm, "end": v(6.6, -63.5) * mm});
            skPoint(sketch, "E6.4.6.0", {"position": v(17.4, -88.01) * mm});
            skLineSegment(sketch, "E6.4.6.1", {"start": v(6.6, -98.8) * mm, "end": v(28.2, -98.8) * mm});
            skLineSegment(sketch, "E6.4.6.2", {"start": v(6.6, -77.22) * mm, "end": v(28.2, -77.22) * mm});
            skLineSegment(sketch, "E6.4.6.3", {"start": v(28.2, -77.22) * mm, "end": v(28.2, -98.8) * mm});
            skLineSegment(sketch, "E6.4.6.4", {"start": v(6.6, -77.22) * mm, "end": v(6.6, -98.8) * mm});
            skPoint(sketch, "E6.4.7.0", {"position": v(17.4, -123.32) * mm});
            skLineSegment(sketch, "E6.4.7.1", {"start": v(6.6, -134.11) * mm, "end": v(28.2, -134.11) * mm});
            skLineSegment(sketch, "E6.4.7.2", {"start": v(6.6, -112.52) * mm, "end": v(28.2, -112.52) * mm});
            skLineSegment(sketch, "E6.4.7.3", {"start": v(28.2, -112.52) * mm, "end": v(28.2, -134.11) * mm});
            skLineSegment(sketch, "E6.4.7.4", {"start": v(6.6, -112.52) * mm, "end": v(6.6, -134.11) * mm});
            skPoint(sketch, "E6.5.0.0", {"position": v(52.7, 123.82) * mm});
            skLineSegment(sketch, "E6.5.0.1", {"start": v(41.91, 113.03) * mm, "end": v(63.5, 113.03) * mm});
            skLineSegment(sketch, "E6.5.0.2", {"start": v(41.91, 134.62) * mm, "end": v(63.5, 134.62) * mm});
            skLineSegment(sketch, "E6.5.0.3", {"start": v(63.5, 134.62) * mm, "end": v(63.5, 113.03) * mm});
            skLineSegment(sketch, "E6.5.0.4", {"start": v(41.91, 134.62) * mm, "end": v(41.91, 113.03) * mm});
            skPoint(sketch, "E6.5.1.0", {"position": v(52.7, 88.52) * mm});
            skLineSegment(sketch, "E6.5.1.1", {"start": v(41.91, 77.72) * mm, "end": v(63.5, 77.72) * mm});
            skLineSegment(sketch, "E6.5.1.2", {"start": v(41.91, 99.31) * mm, "end": v(63.5, 99.31) * mm});
            skLineSegment(sketch, "E6.5.1.3", {"start": v(63.5, 99.31) * mm, "end": v(63.5, 77.72) * mm});
            skLineSegment(sketch, "E6.5.1.4", {"start": v(41.91, 99.31) * mm, "end": v(41.91, 77.72) * mm});
            skPoint(sketch, "E6.5.2.0", {"position": v(52.7, 53.21) * mm});
            skLineSegment(sketch, "E6.5.2.1", {"start": v(41.91, 42.42) * mm, "end": v(63.5, 42.42) * mm});
            skLineSegment(sketch, "E6.5.2.2", {"start": v(41.91, 64) * mm, "end": v(63.5, 64) * mm});
            skLineSegment(sketch, "E6.5.2.3", {"start": v(63.5, 64) * mm, "end": v(63.5, 42.42) * mm});
            skLineSegment(sketch, "E6.5.2.4", {"start": v(41.91, 64) * mm, "end": v(41.91, 42.42) * mm});
            skPoint(sketch, "E6.5.3.0", {"position": v(52.7, 17.9) * mm});
            skLineSegment(sketch, "E6.5.3.1", {"start": v(41.91, 7.11) * mm, "end": v(63.5, 7.11) * mm});
            skLineSegment(sketch, "E6.5.3.2", {"start": v(41.91, 28.7) * mm, "end": v(63.5, 28.7) * mm});
            skLineSegment(sketch, "E6.5.3.3", {"start": v(63.5, 28.7) * mm, "end": v(63.5, 7.11) * mm});
            skLineSegment(sketch, "E6.5.3.4", {"start": v(41.91, 28.7) * mm, "end": v(41.91, 7.11) * mm});
            skPoint(sketch, "E6.5.4.0", {"position": v(52.7, -17.4) * mm});
            skLineSegment(sketch, "E6.5.4.1", {"start": v(41.91, -28.2) * mm, "end": v(63.5, -28.2) * mm});
            skLineSegment(sketch, "E6.5.4.2", {"start": v(41.91, -6.6) * mm, "end": v(63.5, -6.6) * mm});
            skLineSegment(sketch, "E6.5.4.3", {"start": v(63.5, -6.6) * mm, "end": v(63.5, -28.2) * mm});
            skLineSegment(sketch, "E6.5.4.4", {"start": v(41.91, -6.6) * mm, "end": v(41.91, -28.2) * mm});
            skPoint(sketch, "E6.5.5.0", {"position": v(52.7, -52.7) * mm});
            skLineSegment(sketch, "E6.5.5.1", {"start": v(41.91, -63.5) * mm, "end": v(63.5, -63.5) * mm});
            skLineSegment(sketch, "E6.5.5.2", {"start": v(41.91, -41.91) * mm, "end": v(63.5, -41.91) * mm});
            skLineSegment(sketch, "E6.5.5.3", {"start": v(63.5, -41.91) * mm, "end": v(63.5, -63.5) * mm});
            skLineSegment(sketch, "E6.5.5.4", {"start": v(41.91, -41.91) * mm, "end": v(41.91, -63.5) * mm});
            skPoint(sketch, "E6.5.6.0", {"position": v(52.7, -88.01) * mm});
            skLineSegment(sketch, "E6.5.6.1", {"start": v(41.91, -98.8) * mm, "end": v(63.5, -98.8) * mm});
            skLineSegment(sketch, "E6.5.6.2", {"start": v(41.91, -77.22) * mm, "end": v(63.5, -77.22) * mm});
            skLineSegment(sketch, "E6.5.6.3", {"start": v(63.5, -77.22) * mm, "end": v(63.5, -98.8) * mm});
            skLineSegment(sketch, "E6.5.6.4", {"start": v(41.91, -77.22) * mm, "end": v(41.91, -98.8) * mm});
            skPoint(sketch, "E6.5.7.0", {"position": v(52.7, -123.32) * mm});
            skLineSegment(sketch, "E6.5.7.1", {"start": v(41.91, -134.11) * mm, "end": v(63.5, -134.11) * mm});
            skLineSegment(sketch, "E6.5.7.2", {"start": v(41.91, -112.52) * mm, "end": v(63.5, -112.52) * mm});
            skLineSegment(sketch, "E6.5.7.3", {"start": v(63.5, -112.52) * mm, "end": v(63.5, -134.11) * mm});
            skLineSegment(sketch, "E6.5.7.4", {"start": v(41.91, -112.52) * mm, "end": v(41.91, -134.11) * mm});
            skPoint(sketch, "E6.6.0.0", {"position": v(88.01, 123.82) * mm});
            skLineSegment(sketch, "E6.6.0.1", {"start": v(77.22, 113.03) * mm, "end": v(98.8, 113.03) * mm});
            skLineSegment(sketch, "E6.6.0.2", {"start": v(77.22, 134.62) * mm, "end": v(98.8, 134.62) * mm});
            skLineSegment(sketch, "E6.6.0.3", {"start": v(98.8, 134.62) * mm, "end": v(98.8, 113.03) * mm});
            skLineSegment(sketch, "E6.6.0.4", {"start": v(77.22, 134.62) * mm, "end": v(77.22, 113.03) * mm});
            skPoint(sketch, "E6.6.1.0", {"position": v(88.01, 88.52) * mm});
            skLineSegment(sketch, "E6.6.1.1", {"start": v(77.22, 77.72) * mm, "end": v(98.8, 77.72) * mm});
            skLineSegment(sketch, "E6.6.1.2", {"start": v(77.22, 99.31) * mm, "end": v(98.8, 99.31) * mm});
            skLineSegment(sketch, "E6.6.1.3", {"start": v(98.8, 99.31) * mm, "end": v(98.8, 77.72) * mm});
            skLineSegment(sketch, "E6.6.1.4", {"start": v(77.22, 99.31) * mm, "end": v(77.22, 77.72) * mm});
            skPoint(sketch, "E6.6.2.0", {"position": v(88.01, 53.21) * mm});
            skLineSegment(sketch, "E6.6.2.1", {"start": v(77.22, 42.42) * mm, "end": v(98.8, 42.42) * mm});
            skLineSegment(sketch, "E6.6.2.2", {"start": v(77.22, 64) * mm, "end": v(98.8, 64) * mm});
            skLineSegment(sketch, "E6.6.2.3", {"start": v(98.8, 64) * mm, "end": v(98.8, 42.42) * mm});
            skLineSegment(sketch, "E6.6.2.4", {"start": v(77.22, 64) * mm, "end": v(77.22, 42.42) * mm});
            skPoint(sketch, "E6.6.3.0", {"position": v(88.01, 17.9) * mm});
            skLineSegment(sketch, "E6.6.3.1", {"start": v(77.22, 7.11) * mm, "end": v(98.8, 7.11) * mm});
            skLineSegment(sketch, "E6.6.3.2", {"start": v(77.22, 28.7) * mm, "end": v(98.8, 28.7) * mm});
            skLineSegment(sketch, "E6.6.3.3", {"start": v(98.8, 28.7) * mm, "end": v(98.8, 7.11) * mm});
            skLineSegment(sketch, "E6.6.3.4", {"start": v(77.22, 28.7) * mm, "end": v(77.22, 7.11) * mm});
            skPoint(sketch, "E6.6.4.0", {"position": v(88.01, -17.4) * mm});
            skLineSegment(sketch, "E6.6.4.1", {"start": v(77.22, -28.2) * mm, "end": v(98.8, -28.2) * mm});
            skLineSegment(sketch, "E6.6.4.2", {"start": v(77.22, -6.6) * mm, "end": v(98.8, -6.6) * mm});
            skLineSegment(sketch, "E6.6.4.3", {"start": v(98.8, -6.6) * mm, "end": v(98.8, -28.2) * mm});
            skLineSegment(sketch, "E6.6.4.4", {"start": v(77.22, -6.6) * mm, "end": v(77.22, -28.2) * mm});
            skPoint(sketch, "E6.6.5.0", {"position": v(88.01, -52.7) * mm});
            skLineSegment(sketch, "E6.6.5.1", {"start": v(77.22, -63.5) * mm, "end": v(98.8, -63.5) * mm});
            skLineSegment(sketch, "E6.6.5.2", {"start": v(77.22, -41.91) * mm, "end": v(98.8, -41.91) * mm});
            skLineSegment(sketch, "E6.6.5.3", {"start": v(98.8, -41.91) * mm, "end": v(98.8, -63.5) * mm});
            skLineSegment(sketch, "E6.6.5.4", {"start": v(77.22, -41.91) * mm, "end": v(77.22, -63.5) * mm});
            skPoint(sketch, "E6.6.6.0", {"position": v(88.01, -88.01) * mm});
            skLineSegment(sketch, "E6.6.6.1", {"start": v(77.22, -98.8) * mm, "end": v(98.8, -98.8) * mm});
            skLineSegment(sketch, "E6.6.6.2", {"start": v(77.22, -77.22) * mm, "end": v(98.8, -77.22) * mm});
            skLineSegment(sketch, "E6.6.6.3", {"start": v(98.8, -77.22) * mm, "end": v(98.8, -98.8) * mm});
            skLineSegment(sketch, "E6.6.6.4", {"start": v(77.22, -77.22) * mm, "end": v(77.22, -98.8) * mm});
            skPoint(sketch, "E6.6.7.0", {"position": v(88.01, -123.32) * mm});
            skLineSegment(sketch, "E6.6.7.1", {"start": v(77.22, -134.11) * mm, "end": v(98.8, -134.11) * mm});
            skLineSegment(sketch, "E6.6.7.2", {"start": v(77.22, -112.52) * mm, "end": v(98.8, -112.52) * mm});
            skLineSegment(sketch, "E6.6.7.3", {"start": v(98.8, -112.52) * mm, "end": v(98.8, -134.11) * mm});
            skLineSegment(sketch, "E6.6.7.4", {"start": v(77.22, -112.52) * mm, "end": v(77.22, -134.11) * mm});
            skPoint(sketch, "E6.7.0.0", {"position": v(123.32, 123.82) * mm});
            skLineSegment(sketch, "E6.7.0.1", {"start": v(112.52, 113.03) * mm, "end": v(134.11, 113.03) * mm});
            skLineSegment(sketch, "E6.7.0.2", {"start": v(112.52, 134.62) * mm, "end": v(134.11, 134.62) * mm});
            skLineSegment(sketch, "E6.7.0.3", {"start": v(134.11, 134.62) * mm, "end": v(134.11, 113.03) * mm});
            skLineSegment(sketch, "E6.7.0.4", {"start": v(112.52, 134.62) * mm, "end": v(112.52, 113.03) * mm});
            skPoint(sketch, "E6.7.1.0", {"position": v(123.32, 88.52) * mm});
            skLineSegment(sketch, "E6.7.1.1", {"start": v(112.52, 77.72) * mm, "end": v(134.11, 77.72) * mm});
            skLineSegment(sketch, "E6.7.1.2", {"start": v(112.52, 99.31) * mm, "end": v(134.11, 99.31) * mm});
            skLineSegment(sketch, "E6.7.1.3", {"start": v(134.11, 99.31) * mm, "end": v(134.11, 77.72) * mm});
            skLineSegment(sketch, "E6.7.1.4", {"start": v(112.52, 99.31) * mm, "end": v(112.52, 77.72) * mm});
            skPoint(sketch, "E6.7.2.0", {"position": v(123.32, 53.21) * mm});
            skLineSegment(sketch, "E6.7.2.1", {"start": v(112.52, 42.42) * mm, "end": v(134.11, 42.42) * mm});
            skLineSegment(sketch, "E6.7.2.2", {"start": v(112.52, 64) * mm, "end": v(134.11, 64) * mm});
            skLineSegment(sketch, "E6.7.2.3", {"start": v(134.11, 64) * mm, "end": v(134.11, 42.42) * mm});
            skLineSegment(sketch, "E6.7.2.4", {"start": v(112.52, 64) * mm, "end": v(112.52, 42.42) * mm});
            skPoint(sketch, "E6.7.3.0", {"position": v(123.32, 17.9) * mm});
            skLineSegment(sketch, "E6.7.3.1", {"start": v(112.52, 7.11) * mm, "end": v(134.11, 7.11) * mm});
            skLineSegment(sketch, "E6.7.3.2", {"start": v(112.52, 28.7) * mm, "end": v(134.11, 28.7) * mm});
            skLineSegment(sketch, "E6.7.3.3", {"start": v(134.11, 28.7) * mm, "end": v(134.11, 7.11) * mm});
            skLineSegment(sketch, "E6.7.3.4", {"start": v(112.52, 28.7) * mm, "end": v(112.52, 7.11) * mm});
            skPoint(sketch, "E6.7.4.0", {"position": v(123.32, -17.4) * mm});
            skLineSegment(sketch, "E6.7.4.1", {"start": v(112.52, -28.2) * mm, "end": v(134.11, -28.2) * mm});
            skLineSegment(sketch, "E6.7.4.2", {"start": v(112.52, -6.6) * mm, "end": v(134.11, -6.6) * mm});
            skLineSegment(sketch, "E6.7.4.3", {"start": v(134.11, -6.6) * mm, "end": v(134.11, -28.2) * mm});
            skLineSegment(sketch, "E6.7.4.4", {"start": v(112.52, -6.6) * mm, "end": v(112.52, -28.2) * mm});
            skPoint(sketch, "E6.7.5.0", {"position": v(123.32, -52.7) * mm});
            skLineSegment(sketch, "E6.7.5.1", {"start": v(112.52, -63.5) * mm, "end": v(134.11, -63.5) * mm});
            skLineSegment(sketch, "E6.7.5.2", {"start": v(112.52, -41.91) * mm, "end": v(134.11, -41.91) * mm});
            skLineSegment(sketch, "E6.7.5.3", {"start": v(134.11, -41.91) * mm, "end": v(134.11, -63.5) * mm});
            skLineSegment(sketch, "E6.7.5.4", {"start": v(112.52, -41.91) * mm, "end": v(112.52, -63.5) * mm});
            skPoint(sketch, "E6.7.6.0", {"position": v(123.32, -88.01) * mm});
            skLineSegment(sketch, "E6.7.6.1", {"start": v(112.52, -98.8) * mm, "end": v(134.11, -98.8) * mm});
            skLineSegment(sketch, "E6.7.6.2", {"start": v(112.52, -77.22) * mm, "end": v(134.11, -77.22) * mm});
            skLineSegment(sketch, "E6.7.6.3", {"start": v(134.11, -77.22) * mm, "end": v(134.11, -98.8) * mm});
            skLineSegment(sketch, "E6.7.6.4", {"start": v(112.52, -77.22) * mm, "end": v(112.52, -98.8) * mm});
            skPoint(sketch, "E6.7.7.0", {"position": v(123.32, -123.32) * mm});
            skLineSegment(sketch, "E6.7.7.1", {"start": v(112.52, -134.11) * mm, "end": v(134.11, -134.11) * mm});
            skLineSegment(sketch, "E6.7.7.2", {"start": v(112.52, -112.52) * mm, "end": v(134.11, -112.52) * mm});
            skLineSegment(sketch, "E6.7.7.3", {"start": v(134.11, -112.52) * mm, "end": v(134.11, -134.11) * mm});
            skLineSegment(sketch, "E6.7.7.4", {"start": v(112.52, -112.52) * mm, "end": v(112.52, -134.11) * mm});
            skLineSegment(sketch, "E6.direction1", {"start": v(-134.62, 113.03) * mm, "end": v(-99.31, 113.03) * mm, "construction": true});
            skLineSegment(sketch, "E6.direction2", {"start": v(-134.62, 113.03) * mm, "end": v(-134.62, 77.72) * mm, "construction": true});
            skSolve(sketch);
        }
        {
            var Q0;
            Q0 = qSketchRegion(id + "F4", true);
            extrude(context, id + "F5", {"entities" : qUnion([Q0]), "operationType" : NewBodyOperationType.REMOVE, "endBound" : BoundingType.THROUGH_ALL, "oppositeDirection" : true, "depth" : 3.17 * mm});
        }
        {
            var Q0;
            Q0=makeQuery(id+"F1.opExtrude","SWEPT_EDGE",EDGE,{"disambiguationData":[OSD([sQuery(id+"F0.wireOp",EDGE,"E0.top"),sQuery(id+"F0.wireOp",EDGE,"E0.left")])]});
            var Q1;
            Q1=makeQuery(id+"F1.opExtrude","SWEPT_EDGE",EDGE,{"disambiguationData":[OSD([sQuery(id+"F0.wireOp",EDGE,"E0.top"),sQuery(id+"F0.wireOp",EDGE,"E0.right")])]});
            var Q2;
            Q2=makeQuery(id+"F1.opExtrude","SWEPT_EDGE",EDGE,{"disambiguationData":[OSD([sQuery(id+"F0.wireOp",EDGE,"E0.bottom"),sQuery(id+"F0.wireOp",EDGE,"E0.right")])]});
            var Q3;
            Q3=makeQuery(id+"F1.opExtrude","SWEPT_EDGE",EDGE,{"disambiguationData":[OSD([sQuery(id+"F0.wireOp",EDGE,"E0.bottom"),sQuery(id+"F0.wireOp",EDGE,"E0.left")])]});
            chamfer(context, id + "F6", {"entities" : qUnion([Q0, Q1, Q2, Q3]), "width" : 7.62 * mm, "tangentPropagation" : true});
        }
        {
            var Q0;
            Q0=makeQuery(id+"F1.opExtrude","CAP_FACE",FACE,{"disambiguationData":[OSD([sQuery(id+"F0.wireOp",EDGE,"E0.bottom"),sQuery(id+"F0.wireOp",EDGE,"E0.top"),sQuery(id+"F0.wireOp",EDGE,"E0.left"),sQuery(id+"F0.wireOp",EDGE,"E0.right")])],"isStart":true});
            var sketch = newSketch(context, id + "F7", { "sketchPlane" : qUnion([Q0])});
            skLineSegment(sketch, "E7.bottom", {"start": v(-125.1, 125.1) * mm, "end": v(125.1, 125.1) * mm});
            skLineSegment(sketch, "E7.top", {"start": v(-125.1, -125.1) * mm, "end": v(125.1, -125.1) * mm});
            skLineSegment(sketch, "E7.left", {"start": v(-125.1, 125.1) * mm, "end": v(-125.1, -125.1) * mm});
            skLineSegment(sketch, "E7.right", {"start": v(125.1, 125.1) * mm, "end": v(125.1, -125.1) * mm});
            skPoint(sketch, "E7.middle", {"position": v(0, 0) * mm});
            skSolve(sketch);
        }
        {
            var Q0;
            Q0=makeQuery(id+"F7.imprint","IMPRINT",FACE,{"disambiguationData":[TD([[makeQuery(id+"F7.imprint","IMPRINT",EDGE,{"derivedFrom":sQuery(id+"F7.wireOp",EDGE,"E7.bottom")}),-1.0]])]});
            extrude(context, id + "F8", {"entities" : qUnion([Q0]), "operationType" : NewBodyOperationType.ADD, "depth" : 0.03 * mm});
        }
        {
            var Q0;
            Q0=makeQuery(id+"F1.opExtrude","CAP_FACE",FACE,{"disambiguationData":[OSD([sQuery(id+"F0.wireOp",EDGE,"E0.bottom"),sQuery(id+"F0.wireOp",EDGE,"E0.top"),sQuery(id+"F0.wireOp",EDGE,"E0.left"),sQuery(id+"F0.wireOp",EDGE,"E0.right")])],"isStart":false});
            var sketch = newSketch(context, id + "F9", { "sketchPlane" : qUnion([Q0])});
            skLineSegment(sketch, "E8.bottom", {"start": v(-139.7, 139.7) * mm, "end": v(139.2, 139.7) * mm});
            skLineSegment(sketch, "E8.top", {"start": v(-139.7, -139.2) * mm, "end": v(139.2, -139.2) * mm});
            skLineSegment(sketch, "E8.left", {"start": v(-139.7, 139.7) * mm, "end": v(-139.7, -139.2) * mm});
            skLineSegment(sketch, "E8.right", {"start": v(139.2, 139.7) * mm, "end": v(139.2, -139.2) * mm});
            skSolve(sketch);
        }
        {
            var Q0;
            Q0 = qSketchRegion(id + "F9", true);
            var Q1;
            Q1=makeQuery(id+"F3.boolean.opBoolean","COPY",FACE,{"derivedFrom":makeQuery(id+"F3.opExtrude","CAP_FACE",FACE,{"disambiguationData":[OSD([sQuery(id+"F2.wireOp",EDGE,"E3.2.0.0"),sQuery(id+"F2.wireOp",EDGE,"E3.2.0.1"),sQuery(id+"F2.wireOp",EDGE,"E3.2.0.2"),sQuery(id+"F2.wireOp",EDGE,"E3.2.0.3")])],"isStart":false})});
            extrude(context, id + "F10", {"entities" : qUnion([Q0]), "operationType" : NewBodyOperationType.REMOVE, "endBound" : BoundingType.UP_TO_SURFACE, "oppositeDirection" : true, "endBoundEntityFace" : qUnion([Q1]), "depth" : 25.4 * mm});
        }
    });
